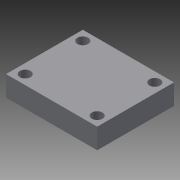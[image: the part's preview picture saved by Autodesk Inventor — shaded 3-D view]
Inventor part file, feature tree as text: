
AUTODESK INVENTOR PART (.ipt)
format: ipt  version: 2015 (Build 190159000, 159)  size: 89,600 bytes
history: native  units: mm
features: sketch x2, other x1, extrude x1, hole x1
ambient origin geometry x8: Origin, YZ Plane, XZ Plane, XY Plane, X Axis, Y Axis, Z Axis, Center Point
bodies: Body1 (feature_tree)
feature tree (5):
  other  "ソリッド1"
  extrude  "押し出し1"  Depth=38.0mm
  hole  "穴1"  [1 undecoded]
  sketch  "スケッチ1"
  sketch  "スケッチ2"
note: 1 required parameter value undecoded (feature->parameter linkage not recoverable at this tier; creation-order binding heuristic only, values carry confidence <= 0.55)
